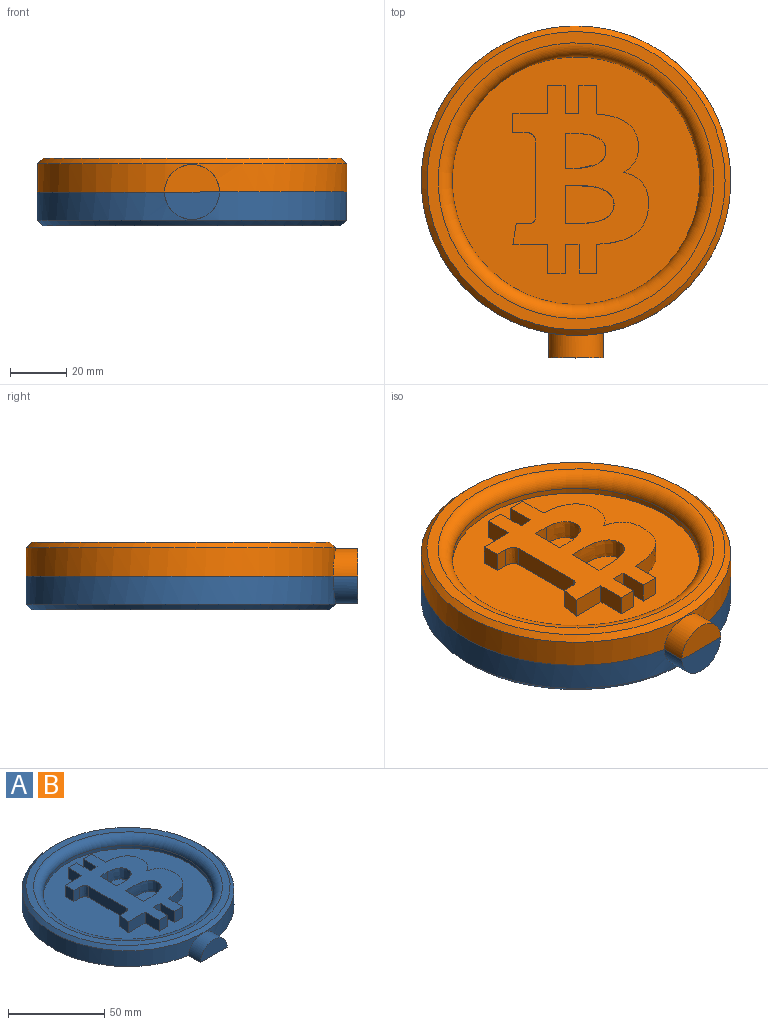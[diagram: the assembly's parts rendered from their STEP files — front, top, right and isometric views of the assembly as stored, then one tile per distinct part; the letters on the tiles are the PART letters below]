
ASSEMBLY  parts=2 mates=1
PART A: 46 faces, bbox 110x118x12 mm
  f0: cylinder r=55mm len=110mm, axis (0,0,-1), area 3306.1mm2, adj f3,f5,f6
  f1: cylinder r=44mm len=88.01mm, axis (0,0,-1), area 553mm2, adj f4,f43
  f2: plane 106x106mm, normal (0,0,1), area 1281mm2, adj f4,f5
  f3: plane 118x110mm, normal (0,0,-1), area 9665mm2, adj f0,f6,f7
  f4: torus R=49mm, axis (0,0,1), area 2261.1mm2, adj f1,f2
  f5: cone r=53mm half-angle=45deg, axis (0,0,-1), area 959.7mm2, adj f0,f2
  f6: cylinder r=9.75mm len=19.5mm, axis (0,1,0), area 271.7mm2, adj f0,f3,f7
  f7: plane 19.5x9.75mm, normal (0,-1,0), area 149.3mm2, adj f3,f6
  f8: extruded ~7x0.26mm, area 1.8mm2, adj f9,f34,f42,f43
  f9: plane 7x4.36mm, normal (0,1,0), area 30.5mm2, adj f8,f35,f42,f43
  f10: plane 10.27x7mm, normal (-1,0,0), area 71.9mm2, adj f11,f41,f42,f43
  f11: plane 7x6.16mm, normal (0,-1,0), area 43.1mm2, adj f10,f12,f42,f43
  f12: plane 10.27x7mm, normal (1,0,0), area 71.9mm2, adj f11,f13,f42,f43
  f13: plane 7x4.95mm, normal (0,-1,0), area 34.6mm2, adj f12,f14,f42,f43
  f14: plane 10.27x7mm, normal (-1,0,0), area 71.9mm2, adj f13,f15,f42,f43
  f15: plane 7x6.13mm, normal (0,-1,0), area 42.9mm2, adj f14,f16,f42,f43
  f16: plane 10.27x7mm, normal (1,0,0), area 71.9mm2, adj f15,f17,f42,f43
  f17: extruded ~18.25x11.11mm, area 163.7mm2, adj f16,f18,f42,f43
  f18: extruded ~7x6.83mm, area 48.1mm2, adj f17,f19,f42,f43
  f19: extruded ~8.58x7.62mm, area 85.1mm2, adj f18,f20,f42,f43
  f20: extruded ~9.38x7mm, area 80.4mm2, adj f19,f21,f42,f43
  f21: extruded ~15.03x11.37mm, area 147.2mm2, adj f20,f22,f42,f43
  f22: plane 10.1x7mm, normal (1,0,0), area 70.7mm2, adj f21,f23,f42,f43
  f23: plane 7x6.14mm, normal (0,1,0), area 43mm2, adj f22,f24,f42,f43
  f24: plane 10.1x7mm, normal (-1,0,0), area 70.7mm2, adj f23,f25,f42,f43
  f25: plane 7x4.93mm, normal (0,1,0), area 34.5mm2, adj f24,f26,f42,f43
  f26: plane 10.1x7mm, normal (1,0,0), area 70.7mm2, adj f25,f27,f42,f43
  f27: plane 7x6.14mm, normal (0,1,0), area 43mm2, adj f26,f28,f42,f43
  f28: plane 10.1x7mm, normal (-1,0,0), area 70.7mm2, adj f27,f29,f42,f43
  f29: plane 12.42x7mm, normal (0,1,0), area 87mm2, adj f28,f30,f42,f43
  f30: plane 7x6.54mm, normal (-1,0,0), area 45.8mm2, adj f29,f31,f42,f43
  f31: plane 7x4.34mm, normal (0,-1,0), area 30.4mm2, adj f30,f32,f42,f43
  f32: extruded ~7x3.69mm, area 35.3mm2, adj f31,f33,f42,f43
  f33: plane 27.68x7mm, normal (-1,0,0), area 193.7mm2, adj f32,f34,f42,f43
  f34: extruded ~7x2.17mm, area 23mm2, adj f8,f33,f42,f43
  f35: plane 7.34x7mm, normal (-0.99,0.17,0), area 52.1mm2, adj f9,f41,f42,f43
  f36: extruded ~17.24x13.63mm, area 292.6mm2, adj f39,f42,f45
  f37: plane 12.28x7mm, normal (1,0,0), area 86mm2, adj f38,f40,f42,f44
  f38: extruded ~7x5.6mm, area 39.2mm2, adj f37,f40,f42,f44
  f39: plane 13.54x7mm, normal (1,0,0), area 94.8mm2, adj f36,f42,f45
  f40: extruded ~14.4x12.29mm, area 206.7mm2, adj f37,f38,f42,f44
  f41: plane 12.42x7mm, normal (0,-1,0), area 86.9mm2, adj f10,f35,f42,f43
  f42: plane 66.69x48.39mm, normal (0,0,1), area 1670.9mm2, adj f8,f9,f10,f11,f12,f13,f14,f15
  f43: plane 88.01x88.01mm, normal (0,0,1), area 4051.3mm2, adj f1,f8,f9,f10,f11,f12,f13,f14
  f44: plane 14.41x12.42mm, normal (0,0,1), area 155mm2, adj f37,f38,f40
  f45: plane 17.31x13.66mm, normal (0,0,1), area 205.2mm2, adj f36,f39
PART B: same geometry as A
PLACE A rot(axis=(0,1,0),180deg) t=(-58.94,-16.48,32.11)mm
PLACE B t=(-58.94,-16.48,32.11)mm
MATE fastened A.f0 <-> B.f0  axis (0,0,1) through (-58.94,-16.48,32.11)mm
